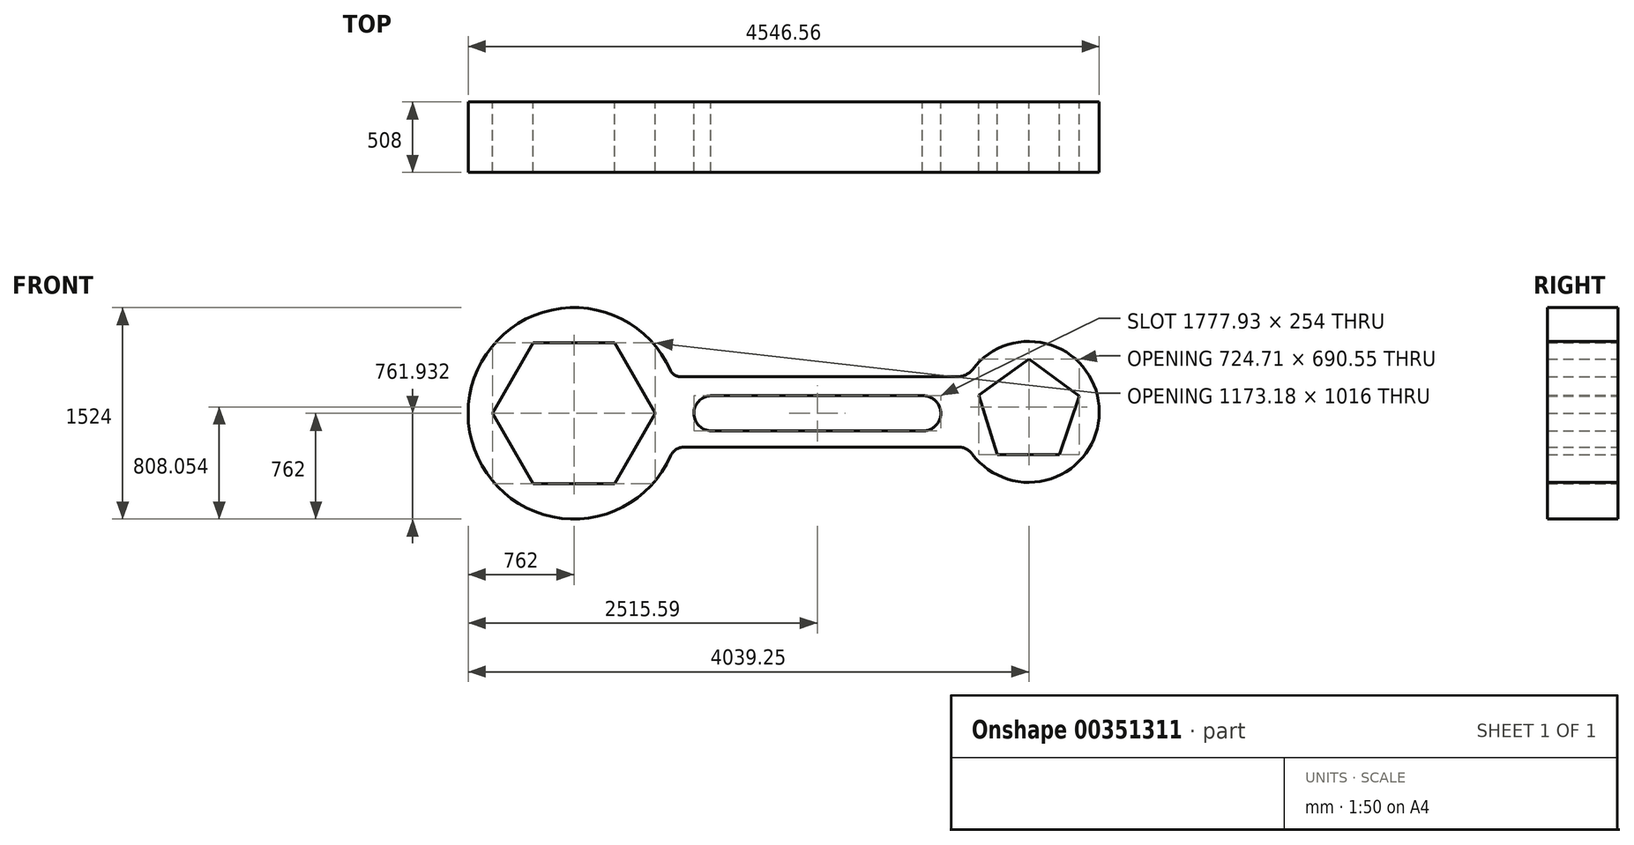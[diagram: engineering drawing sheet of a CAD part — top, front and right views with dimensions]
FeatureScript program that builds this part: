
annotation { "Feature Type Name" : "Feature", "Feature Type Description" : "" }
export const myFeature = defineFeature(function(context is Context, id is Id, definition is map)
    precondition{}
    {
        {
            var Q0;
            Q0=qCreatedBy(makeId("Front.planeOp"),FACE);
            var sketch = newSketch(context, id + "F0", { "sketchPlane" : qUnion([Q0])});
            skCircle(sketch, "E0", {"center": v(-4664.22, 0) * mm, "radius": 762 * mm});
            skCircle(sketch, "E1.cCircle", {"center": v(-4664.22, 0) * mm, "radius": 508 * mm, "construction": true});
            skLineSegment(sketch, "E1.0", {"start": v(-4077.63, 0) * mm, "end": v(-4370.93, -508) * mm});
            skLineSegment(sketch, "E1.1", {"start": v(-4370.93, -508) * mm, "end": v(-4957.51, -508) * mm});
            skLineSegment(sketch, "E1.2", {"start": v(-4957.51, -508) * mm, "end": v(-5250.8, 0) * mm});
            skLineSegment(sketch, "E1.3", {"start": v(-5250.8, 0) * mm, "end": v(-4957.51, 508) * mm});
            skLineSegment(sketch, "E1.4", {"start": v(-4957.51, 508) * mm, "end": v(-4370.93, 508) * mm});
            skLineSegment(sketch, "E1.5", {"start": v(-4370.93, 508) * mm, "end": v(-4077.63, 0) * mm});
            skPoint(sketch, "E1.0.midPoint", {"position": v(-4224.28, -254) * mm});
            skCircle(sketch, "E2", {"center": v(-1387.66, 10.33) * mm, "radius": 508 * mm});
            skCircle(sketch, "E3.cCircle", {"center": v(-1387.66, 10.33) * mm, "radius": 308.24 * mm, "construction": true});
            skLineSegment(sketch, "E3.0", {"start": v(-1165.53, -299.22) * mm, "end": v(-1613.42, -296.6) * mm});
            skLineSegment(sketch, "E3.1", {"start": v(-1613.42, -296.6) * mm, "end": v(-1749.32, 130.2) * mm});
            skLineSegment(sketch, "E3.2", {"start": v(-1749.32, 130.2) * mm, "end": v(-1385.42, 391.33) * mm});
            skLineSegment(sketch, "E3.3", {"start": v(-1385.42, 391.33) * mm, "end": v(-1024.62, 125.94) * mm});
            skLineSegment(sketch, "E3.4", {"start": v(-1024.62, 125.94) * mm, "end": v(-1165.53, -299.22) * mm});
            skPoint(sketch, "E3.0.midPoint", {"position": v(-1389.47, -297.9) * mm});
            skLineSegment(sketch, "E4.0", {"start": v(-4218.2, -243.17) * mm, "end": v(-4218.02, -243.17) * mm});
            skLineSegment(sketch, "E5.0", {"start": v(-4230.72, 264.83) * mm, "end": v(-4230.53, 264.83) * mm});
            skPoint(sketch, "E6.trimOffspring.start.orphan", {"position": v(-3902.22, 0) * mm});
            skPoint(sketch, "E7.orphan", {"position": v(-1895.62, 3.82) * mm});
            skArc(sketch, "E8", {"start": v(-1895.62, 264.83) * mm, "mid": v(-1838.6, 278.27) * mm, "end": v(-1793.6, 315.75) * mm});
            skArc(sketch, "E9", {"start": v(-3968.24, 310.25) * mm, "mid": v(-3939.98, 277.18) * mm, "end": v(-3898.28, 264.83) * mm});
            skArc(sketch, "E10", {"start": v(-3870.93, -243.17) * mm, "mid": v(-3927.79, -260.1) * mm, "end": v(-3966.1, -305.41) * mm});
            skArc(sketch, "E11", {"start": v(-1794.57, -293.8) * mm, "mid": v(-1839.1, -256.53) * mm, "end": v(-1895.62, -243.17) * mm});
            skLineSegment(sketch, "E12.trimOffspring", {"start": v(-3898.28, 264.83) * mm, "end": v(-1895.62, 264.83) * mm});
            skLineSegment(sketch, "E13.trimOffspring", {"start": v(-3870.93, -243.17) * mm, "end": v(-1895.62, -243.17) * mm});
            skLineSegment(sketch, "E14.trimOffspring", {"start": v(-1561.7, 264.83) * mm, "end": v(-1561.56, 264.83) * mm});
            skArc(sketch, "E15", {"start": v(-3678.45, 126.93) * mm, "mid": v(-3799.6, -2.95) * mm, "end": v(-3672.56, -127.07) * mm});
            skArc(sketch, "E16", {"start": v(-2148.7, -127.07) * mm, "mid": v(-2021.66, 2.95) * mm, "end": v(-2154.6, 126.93) * mm});
            skLineSegment(sketch, "E17", {"start": v(-3672.56, -127.07) * mm, "end": v(-2148.7, -127.07) * mm});
            skLineSegment(sketch, "E18", {"start": v(-2154.6, 126.93) * mm, "end": v(-3678.45, 126.93) * mm});
            skSolve(sketch);
        }
        {
            var Q0;
            {var subQ4=sQuery(id+"F0.wireOp",EDGE,"E8");Q0=makeQuery(id+"F0.imprint","IMPRINT",FACE,{"disambiguationData":[TD([[makeQuery(id+"F0.imprint","IMPRINT",EDGE,{"derivedFrom":subQ4}),-1.0]])]});}
            var Q1;
            {var subQ0=sQuery(id+"F0.wireOp",EDGE,"E1.1");Q1=makeQuery(id+"F0.imprint","IMPRINT",FACE,{"disambiguationData":[TD([[makeQuery(id+"F0.imprint","IMPRINT",EDGE,{"derivedFrom":subQ0}),1.0]])]});}
            var Q2;
            Q2=makeQuery(id+"F0.imprint","IMPRINT",FACE,{"disambiguationData":[TD([[makeQuery(id+"F0.imprint","IMPRINT",EDGE,{"derivedFrom":sQuery(id+"F0.wireOp",EDGE,"E3.0")}),1.0]])]});
            extrude(context, id + "F1", {"entities" : qUnion([Q0, Q1, Q2]), "depth" : 508 * mm});
        }
    });
